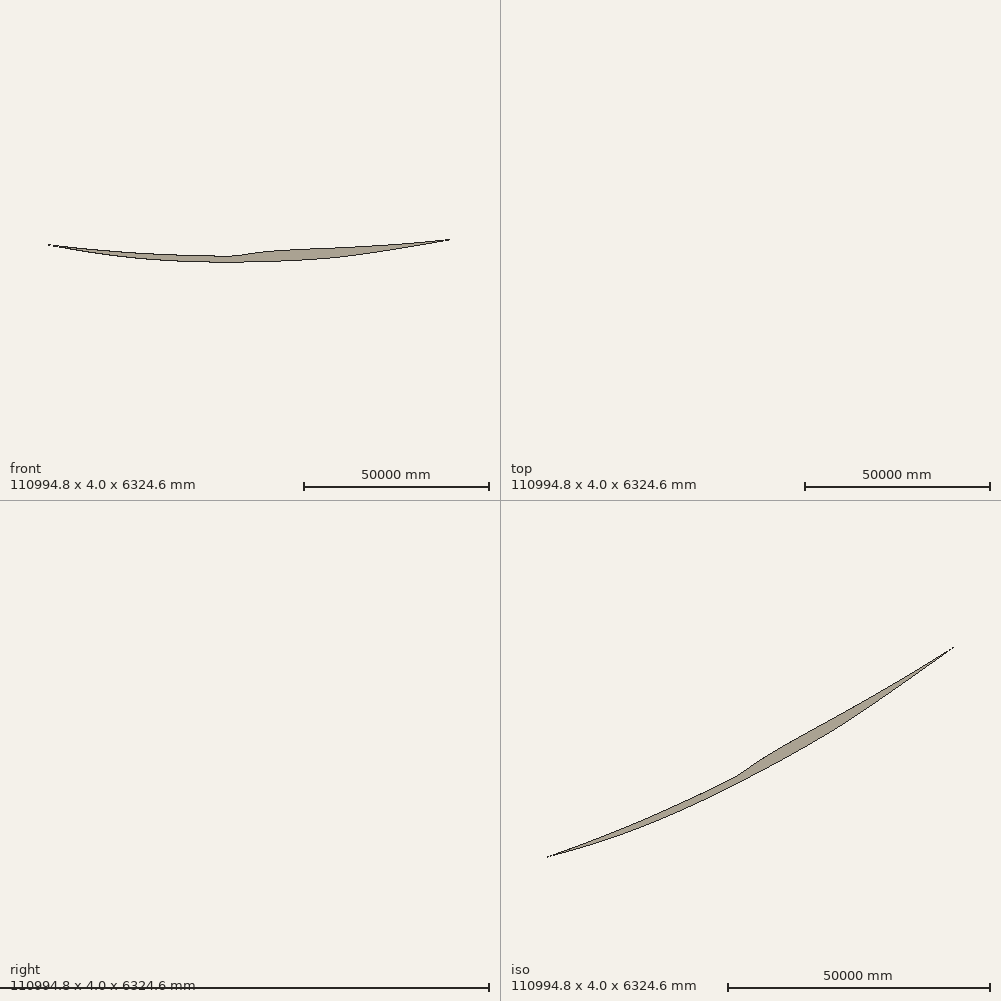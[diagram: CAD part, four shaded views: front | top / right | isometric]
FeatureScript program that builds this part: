
annotation { "Feature Type Name" : "Feature", "Feature Type Description" : "" }
export const myFeature = defineFeature(function(context is Context, id is Id, definition is map)
    precondition{}
    {
        {
            var Q0;
            Q0=qCreatedBy(makeId("Front.planeOp"),FACE);
            var sketch = newSketch(context, id + "F0", { "sketchPlane" : qUnion([Q0])});
            skLineSegment(sketch, "E0", {"start": v(31182.58, 1095.36) * mm, "end": v(31190.9, 968.64) * mm});
            skLineSegment(sketch, "E1", {"start": v(31190.9, 968.64) * mm, "end": v(31182.58, 1095.36) * mm});
            skLineSegment(sketch, "E2", {"start": v(31182.58, 1095.36) * mm, "end": v(31753.29, 1114.6) * mm});
            skLineSegment(sketch, "E3", {"start": v(31753.29, 1114.6) * mm, "end": v(32453.85, 1160.9) * mm});
            skLineSegment(sketch, "E4", {"start": v(32453.85, 1160.9) * mm, "end": v(33153.82, 1217.61) * mm});
            skLineSegment(sketch, "E5", {"start": v(33153.82, 1217.61) * mm, "end": v(34214.98, 1290.97) * mm});
            skLineSegment(sketch, "E6", {"start": v(34214.98, 1290.97) * mm, "end": v(35276.73, 1355.2) * mm});
            skLineSegment(sketch, "E7", {"start": v(35276.73, 1355.2) * mm, "end": v(37666.82, 1511.64) * mm});
            skLineSegment(sketch, "E8", {"start": v(37666.82, 1511.64) * mm, "end": v(39623.07, 1647.96) * mm});
            skLineSegment(sketch, "E9", {"start": v(39623.07, 1647.96) * mm, "end": v(40758.05, 1737.83) * mm});
            skLineSegment(sketch, "E10", {"start": v(40758.05, 1737.83) * mm, "end": v(41892.84, 1829.96) * mm});
            skLineSegment(sketch, "E11", {"start": v(41892.84, 1829.96) * mm, "end": v(42777.07, 1898.9) * mm});
            skLineSegment(sketch, "E12", {"start": v(42777.07, 1898.9) * mm, "end": v(43661.22, 1968.72) * mm});
            skLineSegment(sketch, "E13", {"start": v(43661.22, 1968.72) * mm, "end": v(44940.28, 2078.6) * mm});
            skLineSegment(sketch, "E14", {"start": v(44940.28, 2078.6) * mm, "end": v(45640.46, 2142.68) * mm});
            skLineSegment(sketch, "E15", {"start": v(45640.46, 2142.68) * mm, "end": v(45652.04, 2016.21) * mm});
            skLineSegment(sketch, "E16", {"start": v(45652.04, 2016.21) * mm, "end": v(45640.46, 2142.68) * mm});
            skLineSegment(sketch, "E17", {"start": v(45640.46, 2142.68) * mm, "end": v(46222.53, 2200.7) * mm});
            skLineSegment(sketch, "E18", {"start": v(46222.53, 2200.7) * mm, "end": v(46805.05, 2253.5) * mm});
            skLineSegment(sketch, "E19", {"start": v(46805.05, 2253.5) * mm, "end": v(47563.5, 2312.6) * mm});
            skLineSegment(sketch, "E20", {"start": v(47563.5, 2312.6) * mm, "end": v(48321.76, 2373.44) * mm});
            skLineSegment(sketch, "E21", {"start": v(48321.76, 2373.44) * mm, "end": v(49163.03, 2457.16) * mm});
            skLineSegment(sketch, "E22", {"start": v(49163.03, 2457.16) * mm, "end": v(50003.5, 2549.7) * mm});
            skLineSegment(sketch, "E23", {"start": v(50003.5, 2549.7) * mm, "end": v(51663.74, 2726.42) * mm});
            skLineSegment(sketch, "E24", {"start": v(51663.74, 2726.42) * mm, "end": v(53091.73, 2879.08) * mm});
            skLineSegment(sketch, "E25", {"start": v(53091.73, 2879.08) * mm, "end": v(54204.2, 3001.3) * mm});
            skLineSegment(sketch, "E26", {"start": v(54204.2, 3001.3) * mm, "end": v(54793.58, 3068.43) * mm});
            skLineSegment(sketch, "E27", {"start": v(54793.58, 3068.43) * mm, "end": v(55497.39, 3162.29) * mm});
            skLineSegment(sketch, "E28", {"start": v(55497.39, 3162.29) * mm, "end": v(54815.65, 3032.5) * mm});
            skLineSegment(sketch, "E29", {"start": v(54815.65, 3032.5) * mm, "end": v(54110.4, 2909.13) * mm});
            skLineSegment(sketch, "E30", {"start": v(54110.4, 2909.13) * mm, "end": v(53242.17, 2750.96) * mm});
            skLineSegment(sketch, "E31", {"start": v(53242.17, 2750.96) * mm, "end": v(52374.38, 2590.36) * mm});
            skLineSegment(sketch, "E32", {"start": v(52374.38, 2590.36) * mm, "end": v(51522.72, 2439.86) * mm});
            skLineSegment(sketch, "E33", {"start": v(51522.72, 2439.86) * mm, "end": v(50670.37, 2293.3) * mm});
            skLineSegment(sketch, "E34", {"start": v(50670.37, 2293.3) * mm, "end": v(48651.9, 1945.22) * mm});
            skLineSegment(sketch, "E35", {"start": v(48651.9, 1945.22) * mm, "end": v(46707.92, 1618.37) * mm});
            skLineSegment(sketch, "E36", {"start": v(46707.92, 1618.37) * mm, "end": v(45640.46, 1441.77) * mm});
            skLineSegment(sketch, "E37", {"start": v(45640.46, 1441.77) * mm, "end": v(45619.73, 1567.07) * mm});
            skLineSegment(sketch, "E38", {"start": v(45619.73, 1567.07) * mm, "end": v(45640.46, 1441.77) * mm});
            skLineSegment(sketch, "E39", {"start": v(45640.46, 1441.77) * mm, "end": v(44336.22, 1212.79) * mm});
            skLineSegment(sketch, "E40", {"start": v(44336.22, 1212.79) * mm, "end": v(43030.76, 990.9) * mm});
            skLineSegment(sketch, "E41", {"start": v(43030.76, 990.9) * mm, "end": v(41493.88, 740.27) * mm});
            skLineSegment(sketch, "E42", {"start": v(41493.88, 740.27) * mm, "end": v(39956.65, 491.88) * mm});
            skLineSegment(sketch, "E43", {"start": v(39956.65, 491.88) * mm, "end": v(38660.39, 278.5) * mm});
            skLineSegment(sketch, "E44", {"start": v(38660.39, 278.5) * mm, "end": v(37363.46, 69.46) * mm});
            skLineSegment(sketch, "E45", {"start": v(37363.46, 69.46) * mm, "end": v(36121.23, -120.69) * mm});
            skLineSegment(sketch, "E46", {"start": v(36121.23, -120.69) * mm, "end": v(34879.37, -313.5) * mm});
            skLineSegment(sketch, "E47", {"start": v(34879.37, -313.5) * mm, "end": v(33730.37, -502.35) * mm});
            skLineSegment(sketch, "E48", {"start": v(33730.37, -502.35) * mm, "end": v(32579.86, -680.78) * mm});
            skLineSegment(sketch, "E49", {"start": v(32579.86, -680.78) * mm, "end": v(31682.25, -798.7) * mm});
            skLineSegment(sketch, "E50", {"start": v(31682.25, -798.7) * mm, "end": v(31182.58, -857.42) * mm});
            skLineSegment(sketch, "E51", {"start": v(31182.58, -857.42) * mm, "end": v(31167.77, -731.28) * mm});
            skLineSegment(sketch, "E52", {"start": v(31167.77, -731.28) * mm, "end": v(31182.58, -857.42) * mm});
            skLineSegment(sketch, "E53", {"start": v(31182.58, -857.42) * mm, "end": v(30445.77, -980.7) * mm});
            skLineSegment(sketch, "E54", {"start": v(30445.77, -980.7) * mm, "end": v(29886.67, -1063.94) * mm});
            skLineSegment(sketch, "E55", {"start": v(29886.67, -1063.94) * mm, "end": v(29326.73, -1141.46) * mm});
            skLineSegment(sketch, "E56", {"start": v(29326.73, -1141.46) * mm, "end": v(28107.86, -1303.26) * mm});
            skLineSegment(sketch, "E57", {"start": v(28107.86, -1303.26) * mm, "end": v(26888.1, -1457.77) * mm});
            skLineSegment(sketch, "E58", {"start": v(26888.1, -1457.77) * mm, "end": v(24699.18, -1721.35) * mm});
            skLineSegment(sketch, "E59", {"start": v(24699.18, -1721.35) * mm, "end": v(23828.92, -1823.58) * mm});
            skLineSegment(sketch, "E60", {"start": v(23828.92, -1823.58) * mm, "end": v(22957.52, -1914.33) * mm});
            skLineSegment(sketch, "E61", {"start": v(22957.52, -1914.33) * mm, "end": v(22080.51, -1985.23) * mm});
            skLineSegment(sketch, "E62", {"start": v(22080.51, -1985.23) * mm, "end": v(22070.28, -1858.66) * mm});
            skLineSegment(sketch, "E63", {"start": v(22070.28, -1858.66) * mm, "end": v(22080.51, -1985.23) * mm});
            skLineSegment(sketch, "E64", {"start": v(22080.51, -1985.23) * mm, "end": v(20950.72, -2085.05) * mm});
            skLineSegment(sketch, "E65", {"start": v(20950.72, -2085.05) * mm, "end": v(19027.81, -2241.74) * mm});
            skLineSegment(sketch, "E66", {"start": v(19027.81, -2241.74) * mm, "end": v(17103.3, -2377.22) * mm});
            skLineSegment(sketch, "E67", {"start": v(17103.3, -2377.22) * mm, "end": v(16763.83, -2398.84) * mm});
            skLineSegment(sketch, "E68", {"start": v(16763.83, -2398.84) * mm, "end": v(15626.07, -2478.09) * mm});
            skLineSegment(sketch, "E69", {"start": v(15626.07, -2478.09) * mm, "end": v(14853.96, -2527.95) * mm});
            skLineSegment(sketch, "E70", {"start": v(14853.96, -2527.95) * mm, "end": v(14081.52, -2572.68) * mm});
            skLineSegment(sketch, "E71", {"start": v(14081.52, -2572.68) * mm, "end": v(12409, -2660.46) * mm});
            skLineSegment(sketch, "E72", {"start": v(12409, -2660.46) * mm, "end": v(11151.3, -2725.36) * mm});
            skLineSegment(sketch, "E73", {"start": v(11151.3, -2725.36) * mm, "end": v(9893.39, -2785.73) * mm});
            skLineSegment(sketch, "E74", {"start": v(9893.39, -2785.73) * mm, "end": v(8860.14, -2828.73) * mm});
            skLineSegment(sketch, "E75", {"start": v(8860.14, -2828.73) * mm, "end": v(7826.8, -2869.32) * mm});
            skLineSegment(sketch, "E76", {"start": v(7826.8, -2869.32) * mm, "end": v(7594.1, -2878.6) * mm});
            skLineSegment(sketch, "E77", {"start": v(7594.1, -2878.6) * mm, "end": v(7589.02, -2751.7) * mm});
            skLineSegment(sketch, "E78", {"start": v(7589.02, -2751.7) * mm, "end": v(7594.1, -2878.6) * mm});
            skLineSegment(sketch, "E79", {"start": v(7594.1, -2878.6) * mm, "end": v(5587.1, -2941.28) * mm});
            skLineSegment(sketch, "E80", {"start": v(5587.1, -2941.28) * mm, "end": v(3706.15, -2991.83) * mm});
            skLineSegment(sketch, "E81", {"start": v(3706.15, -2991.83) * mm, "end": v(633.87, -3059.44) * mm});
            skLineSegment(sketch, "E82", {"start": v(633.87, -3059.44) * mm, "end": v(-23.4, -3071.13) * mm});
            skLineSegment(sketch, "E83", {"start": v(-23.4, -3071.13) * mm, "end": v(-1336.38, -3104.73) * mm});
            skLineSegment(sketch, "E84", {"start": v(-1336.38, -3104.73) * mm, "end": v(-2649.54, -3131.3) * mm});
            skLineSegment(sketch, "E85", {"start": v(-2649.54, -3131.3) * mm, "end": v(-4810.14, -3156.52) * mm});
            skLineSegment(sketch, "E86", {"start": v(-4810.14, -3156.52) * mm, "end": v(-6970.9, -3158.53) * mm});
            skLineSegment(sketch, "E87", {"start": v(-6970.9, -3158.53) * mm, "end": v(-7726.06, -3162.29) * mm});
            skLineSegment(sketch, "E88", {"start": v(-7726.06, -3162.29) * mm, "end": v(-8481.23, -3159.75) * mm});
            skLineSegment(sketch, "E89", {"start": v(-8481.23, -3159.75) * mm, "end": v(-9680.08, -3141.15) * mm});
            skLineSegment(sketch, "E90", {"start": v(-9680.08, -3141.15) * mm, "end": v(-10878.9, -3116.97) * mm});
            skLineSegment(sketch, "E91", {"start": v(-10878.9, -3116.97) * mm, "end": v(-11672.35, -3103.71) * mm});
            skLineSegment(sketch, "E92", {"start": v(-11672.35, -3103.71) * mm, "end": v(-12465.7, -3086.95) * mm});
            skLineSegment(sketch, "E93", {"start": v(-12465.7, -3086.95) * mm, "end": v(-13442.15, -3053.45) * mm});
            skLineSegment(sketch, "E94", {"start": v(-13442.15, -3053.45) * mm, "end": v(-13437.78, -2926.52) * mm});
            skLineSegment(sketch, "E95", {"start": v(-13437.78, -2926.52) * mm, "end": v(-13442.15, -3053.45) * mm});
            skLineSegment(sketch, "E96", {"start": v(-13442.15, -3053.45) * mm, "end": v(-14618.7, -3026.78) * mm});
            skLineSegment(sketch, "E97", {"start": v(-14618.7, -3026.78) * mm, "end": v(-15795.1, -2993.15) * mm});
            skLineSegment(sketch, "E98", {"start": v(-15795.1, -2993.15) * mm, "end": v(-18240.36, -2903) * mm});
            skLineSegment(sketch, "E99", {"start": v(-18240.36, -2903) * mm, "end": v(-19558.5, -2849.77) * mm});
            skLineSegment(sketch, "E100", {"start": v(-19558.5, -2849.77) * mm, "end": v(-20876.12, -2786.85) * mm});
            skLineSegment(sketch, "E101", {"start": v(-20876.12, -2786.85) * mm, "end": v(-22678.22, -2677.15) * mm});
            skLineSegment(sketch, "E102", {"start": v(-22678.22, -2677.15) * mm, "end": v(-24480.43, -2566.7) * mm});
            skLineSegment(sketch, "E103", {"start": v(-24480.43, -2566.7) * mm, "end": v(-25106.46, -2532.7) * mm});
            skLineSegment(sketch, "E104", {"start": v(-25106.46, -2532.7) * mm, "end": v(-25732.04, -2492.13) * mm});
            skLineSegment(sketch, "E105", {"start": v(-25732.04, -2492.13) * mm, "end": v(-26486.7, -2424.11) * mm});
            skLineSegment(sketch, "E106", {"start": v(-26486.7, -2424.11) * mm, "end": v(-26475.3, -2297.62) * mm});
            skLineSegment(sketch, "E107", {"start": v(-26475.3, -2297.62) * mm, "end": v(-26486.7, -2424.11) * mm});
            skLineSegment(sketch, "E108", {"start": v(-26486.7, -2424.11) * mm, "end": v(-27325.76, -2367.06) * mm});
            skLineSegment(sketch, "E109", {"start": v(-27325.76, -2367.06) * mm, "end": v(-28164.37, -2303.92) * mm});
            skLineSegment(sketch, "E110", {"start": v(-28164.37, -2303.92) * mm, "end": v(-30245.09, -2118.9) * mm});
            skLineSegment(sketch, "E111", {"start": v(-30245.09, -2118.9) * mm, "end": v(-32323.4, -1907.32) * mm});
            skLineSegment(sketch, "E112", {"start": v(-32323.4, -1907.32) * mm, "end": v(-33590.32, -1771.64) * mm});
            skLineSegment(sketch, "E113", {"start": v(-33590.32, -1771.64) * mm, "end": v(-34856.3, -1627.97) * mm});
            skLineSegment(sketch, "E114", {"start": v(-34856.3, -1627.97) * mm, "end": v(-35959.05, -1493.43) * mm});
            skLineSegment(sketch, "E115", {"start": v(-35959.05, -1493.43) * mm, "end": v(-37061.05, -1352.74) * mm});
            skLineSegment(sketch, "E116", {"start": v(-37061.05, -1352.74) * mm, "end": v(-38157.04, -1209.05) * mm});
            skLineSegment(sketch, "E117", {"start": v(-38157.04, -1209.05) * mm, "end": v(-39252.16, -1058.91) * mm});
            skLineSegment(sketch, "E118", {"start": v(-39252.16, -1058.91) * mm, "end": v(-40134.45, -930.85) * mm});
            skLineSegment(sketch, "E119", {"start": v(-40134.45, -930.85) * mm, "end": v(-41015.9, -796.94) * mm});
            skLineSegment(sketch, "E120", {"start": v(-41015.9, -796.94) * mm, "end": v(-40996.83, -671.39) * mm});
            skLineSegment(sketch, "E121", {"start": v(-40996.83, -671.39) * mm, "end": v(-41015.9, -796.94) * mm});
            skLineSegment(sketch, "E122", {"start": v(-41015.9, -796.94) * mm, "end": v(-42426.52, -606.49) * mm});
            skLineSegment(sketch, "E123", {"start": v(-42426.52, -606.49) * mm, "end": v(-43834.95, -400.5) * mm});
            skLineSegment(sketch, "E124", {"start": v(-43834.95, -400.5) * mm, "end": v(-45389.28, -153.91) * mm});
            skLineSegment(sketch, "E125", {"start": v(-45389.28, -153.91) * mm, "end": v(-46941.3, 106.97) * mm});
            skLineSegment(sketch, "E126", {"start": v(-46941.3, 106.97) * mm, "end": v(-49545.53, 562.57) * mm});
            skLineSegment(sketch, "E127", {"start": v(-49545.53, 562.57) * mm, "end": v(-51072.96, 835.55) * mm});
            skLineSegment(sketch, "E128", {"start": v(-51072.96, 835.55) * mm, "end": v(-52752.38, 1133.67) * mm});
            skLineSegment(sketch, "E129", {"start": v(-52752.38, 1133.67) * mm, "end": v(-54306.94, 1418.48) * mm});
            skLineSegment(sketch, "E130", {"start": v(-54306.94, 1418.48) * mm, "end": v(-55497.39, 1638.29) * mm});
            skLineSegment(sketch, "E131", {"start": v(-55497.39, 1638.29) * mm, "end": v(-54617.1, 1529.47) * mm});
            skLineSegment(sketch, "E132", {"start": v(-54617.1, 1529.47) * mm, "end": v(-53786.34, 1437.98) * mm});
            skLineSegment(sketch, "E133", {"start": v(-53786.34, 1437.98) * mm, "end": v(-52955.66, 1345.8) * mm});
            skLineSegment(sketch, "E134", {"start": v(-52955.66, 1345.8) * mm, "end": v(-51937.65, 1217.59) * mm});
            skLineSegment(sketch, "E135", {"start": v(-51937.65, 1217.59) * mm, "end": v(-50919.27, 1093.23) * mm});
            skLineSegment(sketch, "E136", {"start": v(-50919.27, 1093.23) * mm, "end": v(-50322.62, 1031.6) * mm});
            skLineSegment(sketch, "E137", {"start": v(-50322.62, 1031.6) * mm, "end": v(-49725.64, 972.53) * mm});
            skLineSegment(sketch, "E138", {"start": v(-49725.64, 972.53) * mm, "end": v(-48625.72, 852.92) * mm});
            skLineSegment(sketch, "E139", {"start": v(-48625.72, 852.92) * mm, "end": v(-47526.05, 731.38) * mm});
            skLineSegment(sketch, "E140", {"start": v(-47526.05, 731.38) * mm, "end": v(-46247.37, 604.43) * mm});
            skLineSegment(sketch, "E141", {"start": v(-46247.37, 604.43) * mm, "end": v(-44968.66, 476.85) * mm});
            skLineSegment(sketch, "E142", {"start": v(-44968.66, 476.85) * mm, "end": v(-44112.5, 383.35) * mm});
            skLineSegment(sketch, "E143", {"start": v(-44112.5, 383.35) * mm, "end": v(-43255.6, 298.1) * mm});
            skLineSegment(sketch, "E144", {"start": v(-43255.6, 298.1) * mm, "end": v(-42615.45, 247.28) * mm});
            skLineSegment(sketch, "E145", {"start": v(-42615.45, 247.28) * mm, "end": v(-41975.5, 194.37) * mm});
            skLineSegment(sketch, "E146", {"start": v(-41975.5, 194.37) * mm, "end": v(-41483.24, 145.12) * mm});
            skLineSegment(sketch, "E147", {"start": v(-41483.24, 145.12) * mm, "end": v(-40990.66, 99.86) * mm});
            skLineSegment(sketch, "E148", {"start": v(-40990.66, 99.86) * mm, "end": v(-40889.21, 92.32) * mm});
            skLineSegment(sketch, "E149", {"start": v(-40889.21, 92.32) * mm, "end": v(-40898.61, -34.33) * mm});
            skLineSegment(sketch, "E150", {"start": v(-40898.61, -34.33) * mm, "end": v(-40889.21, 92.32) * mm});
            skLineSegment(sketch, "E151", {"start": v(-40889.21, 92.32) * mm, "end": v(-40038.7, 22.06) * mm});
            skLineSegment(sketch, "E152", {"start": v(-40038.7, 22.06) * mm, "end": v(-38275.7, -128.64) * mm});
            skLineSegment(sketch, "E153", {"start": v(-38275.7, -128.64) * mm, "end": v(-36198.5, -297.45) * mm});
            skLineSegment(sketch, "E154", {"start": v(-36198.5, -297.45) * mm, "end": v(-34602.25, -427.32) * mm});
            skLineSegment(sketch, "E155", {"start": v(-34602.25, -427.32) * mm, "end": v(-33184.4, -536.23) * mm});
            skLineSegment(sketch, "E156", {"start": v(-33184.4, -536.23) * mm, "end": v(-32256.26, -595.85) * mm});
            skLineSegment(sketch, "E157", {"start": v(-32256.26, -595.85) * mm, "end": v(-31328, -653.43) * mm});
            skLineSegment(sketch, "E158", {"start": v(-31328, -653.43) * mm, "end": v(-29812.45, -761.25) * mm});
            skLineSegment(sketch, "E159", {"start": v(-29812.45, -761.25) * mm, "end": v(-29081.39, -816.42) * mm});
            skLineSegment(sketch, "E160", {"start": v(-29081.39, -816.42) * mm, "end": v(-28349.94, -866.03) * mm});
            skLineSegment(sketch, "E161", {"start": v(-28349.94, -866.03) * mm, "end": v(-27418.68, -912.15) * mm});
            skLineSegment(sketch, "E162", {"start": v(-27418.68, -912.15) * mm, "end": v(-26486.7, -940.55) * mm});
            skLineSegment(sketch, "E163", {"start": v(-26486.7, -940.55) * mm, "end": v(-26490.56, -1067.5) * mm});
            skLineSegment(sketch, "E164", {"start": v(-26490.56, -1067.5) * mm, "end": v(-26486.7, -940.55) * mm});
            skLineSegment(sketch, "E165", {"start": v(-26486.7, -940.55) * mm, "end": v(-25098.9, -1007.94) * mm});
            skLineSegment(sketch, "E166", {"start": v(-25098.9, -1007.94) * mm, "end": v(-23787.6, -1061.3) * mm});
            skLineSegment(sketch, "E167", {"start": v(-23787.6, -1061.3) * mm, "end": v(-22476.22, -1112.74) * mm});
            skLineSegment(sketch, "E168", {"start": v(-22476.22, -1112.74) * mm, "end": v(-21366.67, -1160.95) * mm});
            skLineSegment(sketch, "E169", {"start": v(-21366.67, -1160.95) * mm, "end": v(-20257.12, -1209.18) * mm});
            skLineSegment(sketch, "E170", {"start": v(-20257.12, -1209.18) * mm, "end": v(-19236.37, -1248.4) * mm});
            skLineSegment(sketch, "E171", {"start": v(-19236.37, -1248.4) * mm, "end": v(-18215.4, -1280.68) * mm});
            skLineSegment(sketch, "E172", {"start": v(-18215.4, -1280.68) * mm, "end": v(-17168.86, -1307) * mm});
            skLineSegment(sketch, "E173", {"start": v(-17168.86, -1307) * mm, "end": v(-16122.33, -1333.77) * mm});
            skLineSegment(sketch, "E174", {"start": v(-16122.33, -1333.77) * mm, "end": v(-14611.62, -1382.61) * mm});
            skLineSegment(sketch, "E175", {"start": v(-14611.62, -1382.61) * mm, "end": v(-13458.71, -1419.7) * mm});
            skLineSegment(sketch, "E176", {"start": v(-13458.71, -1419.7) * mm, "end": v(-13462.8, -1546.62) * mm});
            skLineSegment(sketch, "E177", {"start": v(-13462.8, -1546.62) * mm, "end": v(-13458.71, -1419.7) * mm});
            skLineSegment(sketch, "E178", {"start": v(-13458.71, -1419.7) * mm, "end": v(-12531.94, -1428.23) * mm});
            skLineSegment(sketch, "E179", {"start": v(-12531.94, -1428.23) * mm, "end": v(-11605.25, -1443.11) * mm});
            skLineSegment(sketch, "E180", {"start": v(-11605.25, -1443.11) * mm, "end": v(-10611.62, -1467.47) * mm});
            skLineSegment(sketch, "E181", {"start": v(-10611.62, -1467.47) * mm, "end": v(-9618, -1490.64) * mm});
            skLineSegment(sketch, "E182", {"start": v(-9618, -1490.64) * mm, "end": v(-8266.67, -1506.28) * mm});
            skLineSegment(sketch, "E183", {"start": v(-8266.67, -1506.28) * mm, "end": v(-7791.41, -1510.14) * mm});
            skLineSegment(sketch, "E184", {"start": v(-7791.41, -1510.14) * mm, "end": v(-6970.9, -1521.12) * mm});
            skLineSegment(sketch, "E185", {"start": v(-6970.9, -1521.12) * mm, "end": v(-6118.21, -1514.9) * mm});
            skLineSegment(sketch, "E186", {"start": v(-6118.21, -1514.9) * mm, "end": v(-5265.43, -1497.27) * mm});
            skLineSegment(sketch, "E187", {"start": v(-5265.43, -1497.27) * mm, "end": v(-4442.02, -1472.07) * mm});
            skLineSegment(sketch, "E188", {"start": v(-4442.02, -1472.07) * mm, "end": v(-3620.6, -1420.5) * mm});
            skLineSegment(sketch, "E189", {"start": v(-3620.6, -1420.5) * mm, "end": v(-2874.15, -1336.05) * mm});
            skLineSegment(sketch, "E190", {"start": v(-2874.15, -1336.05) * mm, "end": v(-2130.34, -1225.51) * mm});
            skLineSegment(sketch, "E191", {"start": v(-2130.34, -1225.51) * mm, "end": v(-1387.84, -1104.35) * mm});
            skLineSegment(sketch, "E192", {"start": v(-1387.84, -1104.35) * mm, "end": v(-683.04, -989.98) * mm});
            skLineSegment(sketch, "E193", {"start": v(-683.04, -989.98) * mm, "end": v(20.97, -872.05) * mm});
            skLineSegment(sketch, "E194", {"start": v(20.97, -872.05) * mm, "end": v(339.94, -823.81) * mm});
            skLineSegment(sketch, "E195", {"start": v(339.94, -823.81) * mm, "end": v(1528, -649.34) * mm});
            skLineSegment(sketch, "E196", {"start": v(1528, -649.34) * mm, "end": v(2718.37, -492.19) * mm});
            skLineSegment(sketch, "E197", {"start": v(2718.37, -492.19) * mm, "end": v(3774.27, -375.8) * mm});
            skLineSegment(sketch, "E198", {"start": v(3774.27, -375.8) * mm, "end": v(4831.9, -275.4) * mm});
            skLineSegment(sketch, "E199", {"start": v(4831.9, -275.4) * mm, "end": v(5862.87, -186.25) * mm});
            skLineSegment(sketch, "E200", {"start": v(5862.87, -186.25) * mm, "end": v(6894.33, -104.13) * mm});
            skLineSegment(sketch, "E201", {"start": v(6894.33, -104.13) * mm, "end": v(7594.1, -52.39) * mm});
            skLineSegment(sketch, "E202", {"start": v(7594.1, -52.39) * mm, "end": v(7603.45, -179.03) * mm});
            skLineSegment(sketch, "E203", {"start": v(7603.45, -179.03) * mm, "end": v(7594.1, -52.39) * mm});
            skLineSegment(sketch, "E204", {"start": v(7594.1, -52.39) * mm, "end": v(8217.65, -4.71) * mm});
            skLineSegment(sketch, "E205", {"start": v(8217.65, -4.71) * mm, "end": v(8841.65, 37.05) * mm});
            skLineSegment(sketch, "E206", {"start": v(8841.65, 37.05) * mm, "end": v(9756.5, 87.06) * mm});
            skLineSegment(sketch, "E207", {"start": v(9756.5, 87.06) * mm, "end": v(10671.6, 133.49) * mm});
            skLineSegment(sketch, "E208", {"start": v(10671.6, 133.49) * mm, "end": v(11617.31, 187.13) * mm});
            skLineSegment(sketch, "E209", {"start": v(11617.31, 187.13) * mm, "end": v(12563.08, 239.03) * mm});
            skLineSegment(sketch, "E210", {"start": v(12563.08, 239.03) * mm, "end": v(13483.83, 279.84) * mm});
            skLineSegment(sketch, "E211", {"start": v(13483.83, 279.84) * mm, "end": v(14404.8, 316.32) * mm});
            skLineSegment(sketch, "E212", {"start": v(14404.8, 316.32) * mm, "end": v(16231.1, 399.22) * mm});
            skLineSegment(sketch, "E213", {"start": v(16231.1, 399.22) * mm, "end": v(17060.99, 442.81) * mm});
            skLineSegment(sketch, "E214", {"start": v(17060.99, 442.81) * mm, "end": v(17891.09, 482.08) * mm});
            skLineSegment(sketch, "E215", {"start": v(17891.09, 482.08) * mm, "end": v(19226, 524.45) * mm});
            skLineSegment(sketch, "E216", {"start": v(19226, 524.45) * mm, "end": v(19824.64, 541.31) * mm});
            skLineSegment(sketch, "E217", {"start": v(19824.64, 541.31) * mm, "end": v(20422.93, 565.75) * mm});
            skLineSegment(sketch, "E218", {"start": v(20422.93, 565.75) * mm, "end": v(21002.87, 599.7) * mm});
            skLineSegment(sketch, "E219", {"start": v(21002.87, 599.7) * mm, "end": v(21583, 627.19) * mm});
            skLineSegment(sketch, "E220", {"start": v(21583, 627.19) * mm, "end": v(22080.51, 633.82) * mm});
            skLineSegment(sketch, "E221", {"start": v(22080.51, 633.82) * mm, "end": v(22082.21, 506.82) * mm});
            skLineSegment(sketch, "E222", {"start": v(22082.21, 506.82) * mm, "end": v(22080.51, 633.82) * mm});
            skLineSegment(sketch, "E223", {"start": v(22080.51, 633.82) * mm, "end": v(23677.84, 706.8) * mm});
            skLineSegment(sketch, "E224", {"start": v(23677.84, 706.8) * mm, "end": v(26295.7, 834.17) * mm});
            skLineSegment(sketch, "E225", {"start": v(26295.7, 834.17) * mm, "end": v(28245.7, 934.96) * mm});
            skLineSegment(sketch, "E226", {"start": v(28245.7, 934.96) * mm, "end": v(29669.32, 1010.86) * mm});
            skLineSegment(sketch, "E227", {"start": v(29669.32, 1010.86) * mm, "end": v(30209.35, 1037.42) * mm});
            skLineSegment(sketch, "E228", {"start": v(30209.35, 1037.42) * mm, "end": v(30749.2, 1066.89) * mm});
            skLineSegment(sketch, "E229", {"start": v(30749.2, 1066.89) * mm, "end": v(31182.58, 1095.36) * mm});
            skSolve(sketch);
        }
        {
            var Q0;
            Q0 = qSketchRegion(id + "F0", true);
            extrude(context, id + "F1", {"entities" : qUnion([Q0]), "depth" : 4 * mm, "offsetDistance" : 25 * mm});
        }
    });
